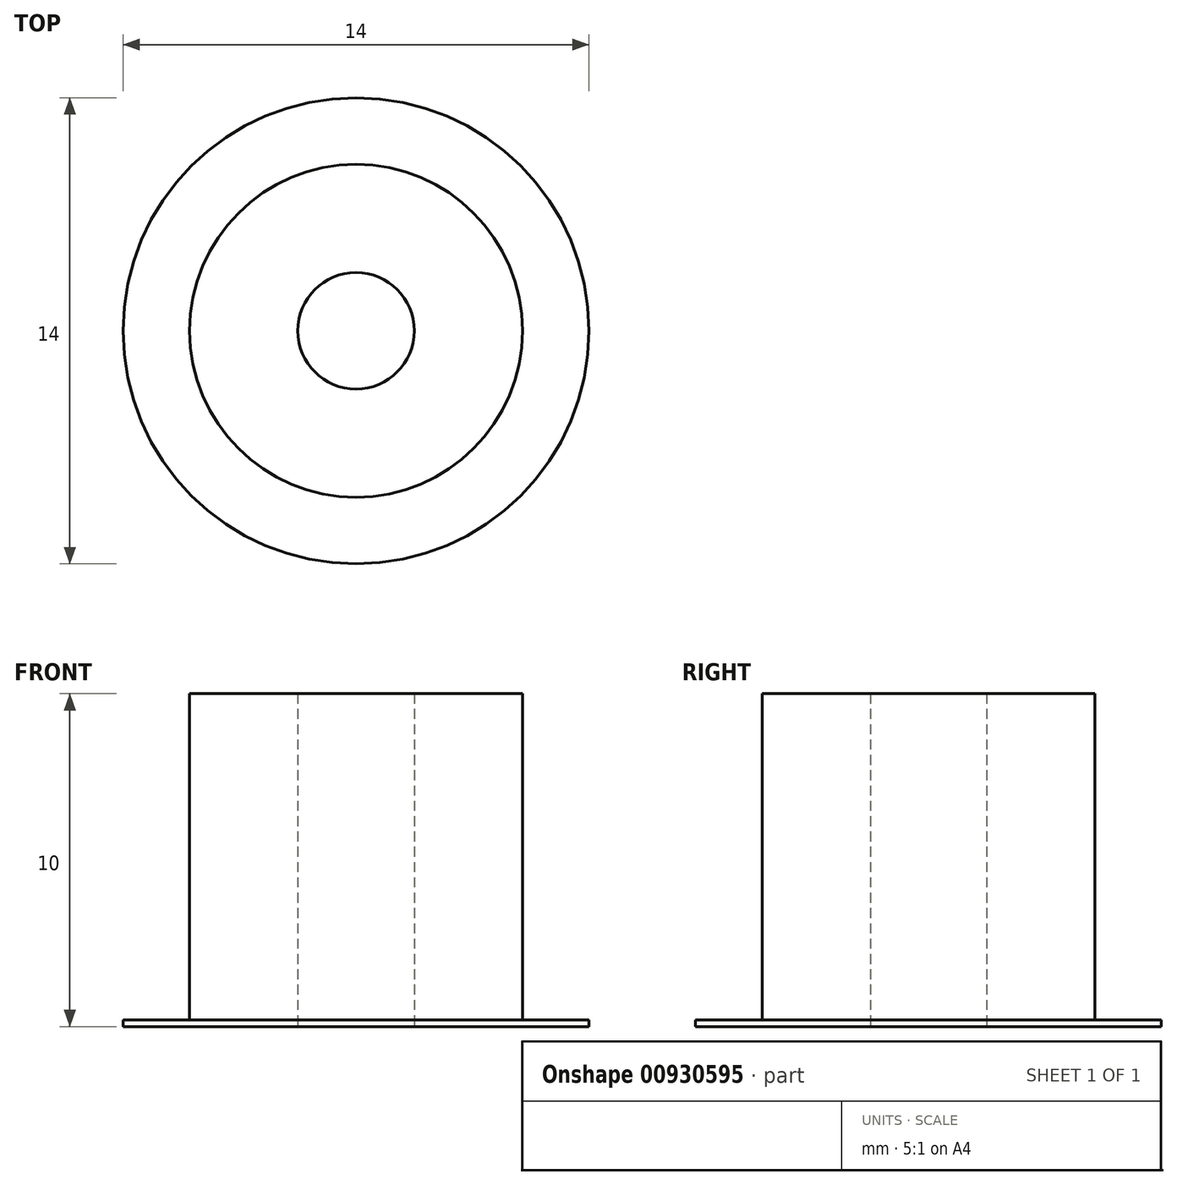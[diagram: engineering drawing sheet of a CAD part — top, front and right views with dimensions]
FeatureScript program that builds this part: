
annotation { "Feature Type Name" : "Feature", "Feature Type Description" : "" }
export const myFeature = defineFeature(function(context is Context, id is Id, definition is map)
    precondition{}
    {
        {
            var Q0;
            Q0=qCreatedBy(makeId("Top.planeOp"),FACE);
            var sketch = newSketch(context, id + "F0", { "sketchPlane" : qUnion([Q0])});
            skCircle(sketch, "E0", {"center": v(0, 0) * mm, "radius": 5 * mm});
            skCircle(sketch, "E1", {"center": v(0, 0) * mm, "radius": 1.75 * mm});
            skSolve(sketch);
        }
        {
            var Q0;
            Q0=qSketchRegion(id+"F0",true);
            extrude(context, id + "F1", {"entities" : qUnion([Q0]), "depth" : 10 * mm});
        }
        {
            var Q0;
            Q0=makeQuery(id+"F1.opExtrude","CAP_FACE",FACE,{"disambiguationData":[OSD([sQuery(id+"F0.wireOp",EDGE,"E0"),sQuery(id+"F0.wireOp",EDGE,"E1")])],"isStart":true});
            var sketch = newSketch(context, id + "F2", { "sketchPlane" : qUnion([Q0])});
            skCircle(sketch, "E2", {"center": v(0, 0) * mm, "radius": 7 * mm});
            skCircle(sketch, "E3", {"center": v(0, 0) * mm, "radius": 5 * mm});
            skSolve(sketch);
        }
        {
            var Q0;
            Q0=qSketchRegion(id+"F2",true);
            extrude(context, id + "F3", {"entities" : qUnion([Q0]), "operationType" : NewBodyOperationType.ADD, "oppositeDirection" : true, "depth" : 0.2 * mm, "offsetDistance" : 25 * mm});
        }
    });
